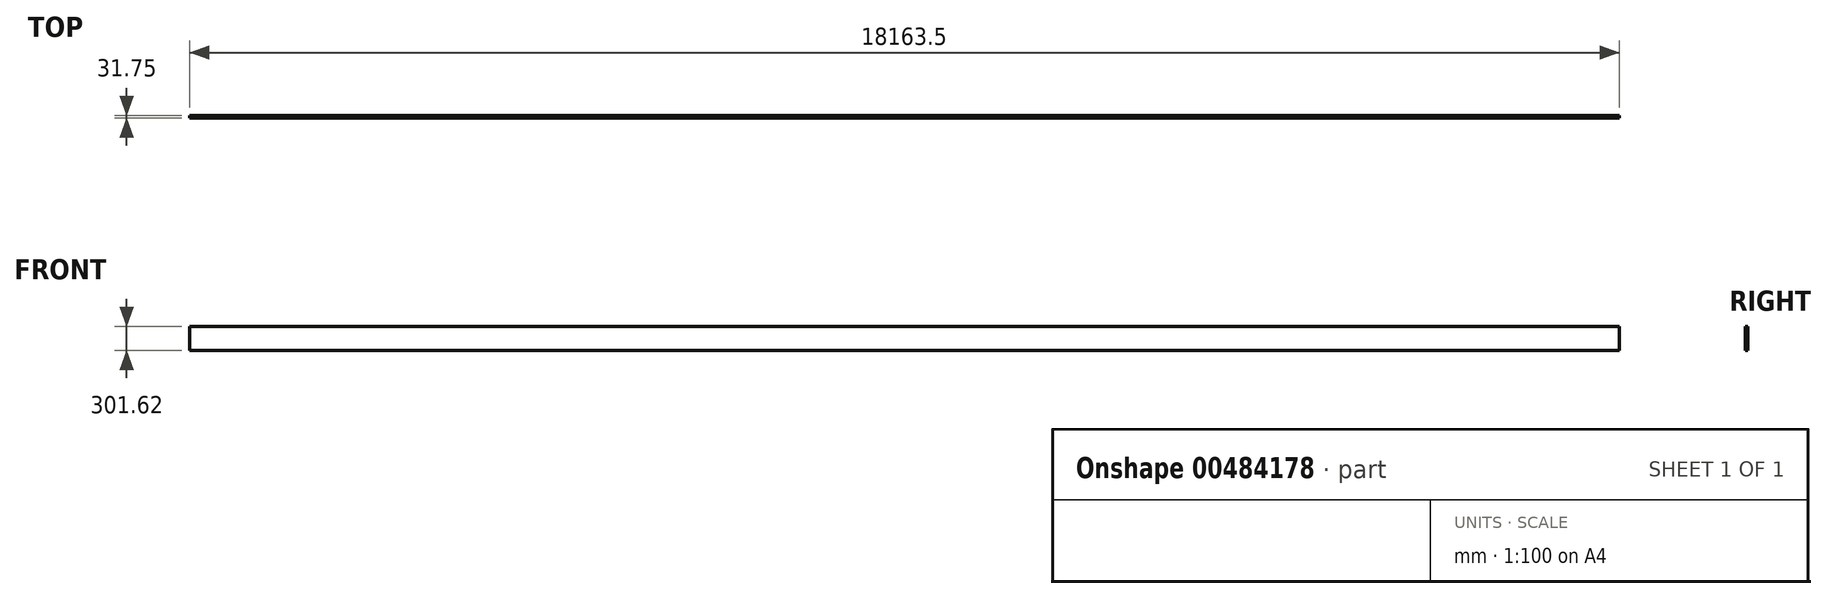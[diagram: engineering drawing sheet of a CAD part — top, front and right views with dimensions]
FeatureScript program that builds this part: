
annotation { "Feature Type Name" : "Feature", "Feature Type Description" : "" }
export const myFeature = defineFeature(function(context is Context, id is Id, definition is map)
    precondition{}
    {
        {
            var Q0;
            Q0=qCreatedBy(makeId("Right.planeOp"),FACE);
            var sketch = newSketch(context, id + "F0", { "sketchPlane" : qUnion([Q0])});
            skLineSegment(sketch, "E0.bottom", {"start": v(0, 0) * mm, "end": v(31.75, 0) * mm});
            skLineSegment(sketch, "E0.top", {"start": v(0, 301.62) * mm, "end": v(31.75, 301.62) * mm});
            skLineSegment(sketch, "E0.left", {"start": v(0, 0) * mm, "end": v(0, 301.62) * mm});
            skLineSegment(sketch, "E0.right", {"start": v(31.75, 0) * mm, "end": v(31.75, 301.63) * mm});
            skSolve(sketch);
        }
        {
            var Q0;
            Q0 = qSketchRegion(id + "F0", true);
            extrude(context, id + "F1", {"entities" : qUnion([Q0]), "depth" : 18163.54 * mm});
        }
    });
